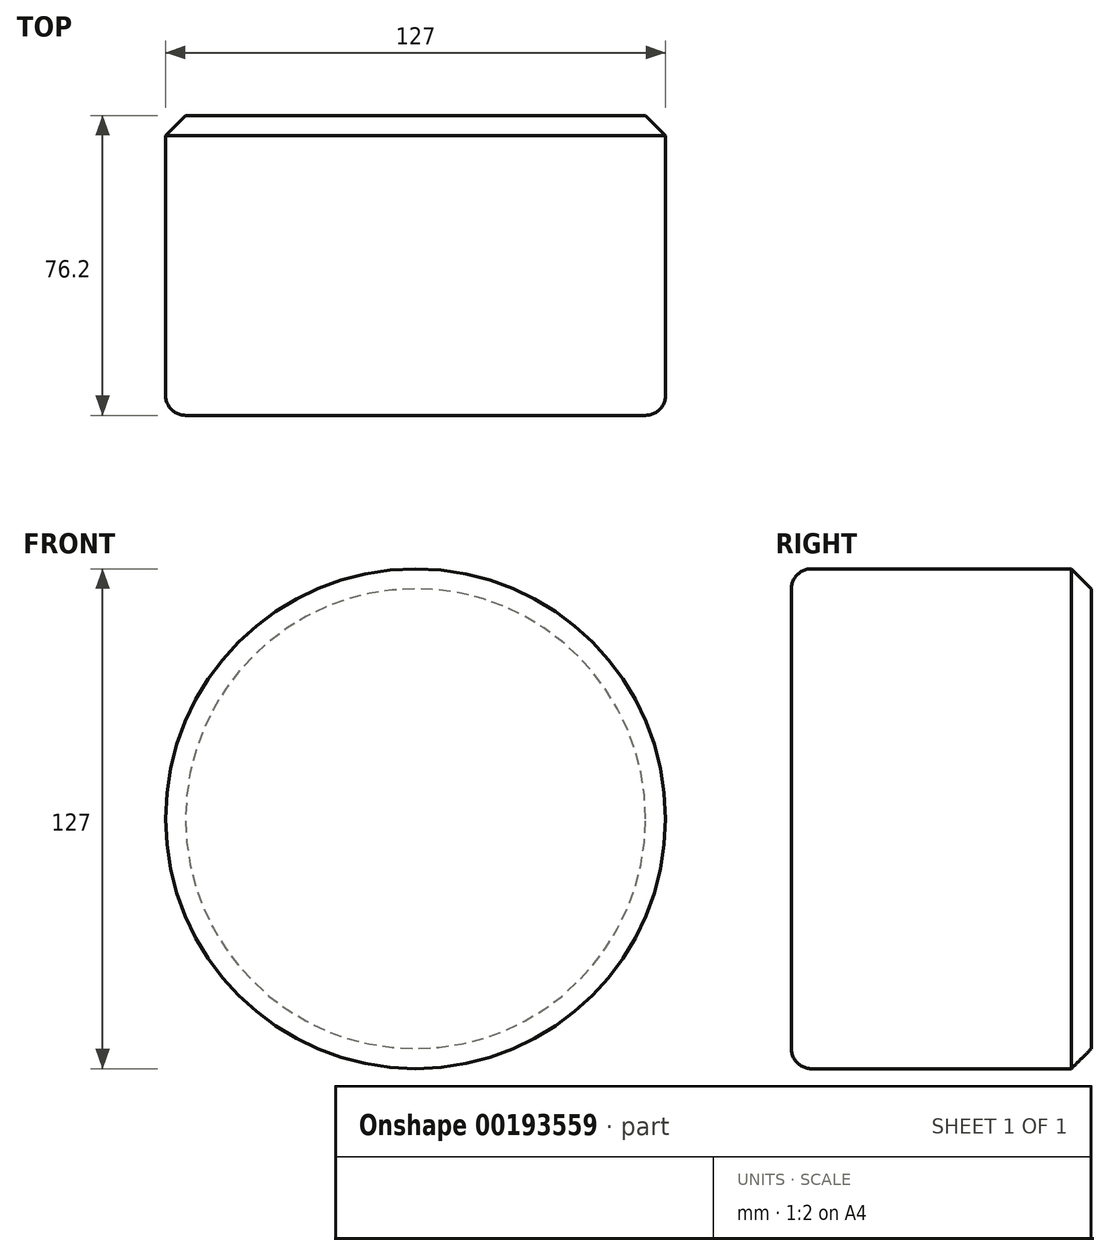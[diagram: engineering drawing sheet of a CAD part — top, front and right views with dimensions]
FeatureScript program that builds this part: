
annotation { "Feature Type Name" : "Feature", "Feature Type Description" : "" }
export const myFeature = defineFeature(function(context is Context, id is Id, definition is map)
    precondition{}
    {
        {
            var Q0;
            Q0=qCreatedBy(makeId("Front.planeOp"),FACE);
            var sketch = newSketch(context, id + "F0", { "sketchPlane" : qUnion([Q0])});
            skCircle(sketch, "E0", {"center": v(0, 0) * mm, "radius": 63.5 * mm});
            skSolve(sketch);
        }
        {
            var Q0;
            Q0=makeQuery(id+"F0.imprint","IMPRINT",FACE,{"disambiguationData":[TD([[makeQuery(id+"F0.imprint","IMPRINT",EDGE,{"derivedFrom":sQuery(id+"F0.wireOp",EDGE,"E0")}),1.0]])]});
            extrude(context, id + "F1", {"entities" : qUnion([Q0]), "depth" : 76.2 * mm});
        }
        {
            var Q0;
            Q0=qCreatedBy(makeId("Front.planeOp"),FACE);
            var sketch = newSketch(context, id + "F2", { "sketchPlane" : qUnion([Q0])});
            skCircle(sketch, "E1", {"center": v(0, 0) * mm, "radius": 30.95 * mm});
            skSolve(sketch);
        }
        {
            var Q0;
            Q0=sQuery(id+"F2.wireOp",EDGE,"E1");
            extrude(context, id + "F3", {"bodyType" : ToolBodyType.SURFACE, "surfaceEntities" : qUnion([Q0]), "depth" : 76.2 * mm});
        }
        {
            var Q0;
            Q0=qCreatedBy(makeId("Front.planeOp"),FACE);
            var sketch = newSketch(context, id + "F4", { "sketchPlane" : qUnion([Q0])});
            skCircle(sketch, "E2", {"center": v(0, 0) * mm, "radius": 9.2 * mm});
            skSolve(sketch);
        }
        {
            var Q0;
            Q0=sQuery(id+"F4.wireOp",EDGE,"E2");
            extrude(context, id + "F5", {"bodyType" : ToolBodyType.SURFACE, "surfaceEntities" : qUnion([Q0]), "depth" : 76.2 * mm});
        }
        {
            var Q0;
            Q0=makeQuery(id+"F1.opExtrude","CAP_EDGE",EDGE,{"disambiguationData":[OSD([sQuery(id+"F0.wireOp",EDGE,"E0")])],"isStart":false});
            fillet(context, id + "F6", {"entities" : qUnion([Q0]), "radius" : 5.08 * mm, "tangentPropagation" : true, "allowEdgeOverflow" : false});
        }
        {
            var Q0;
            Q0=makeQuery(id+"F1.opExtrude","CAP_EDGE",EDGE,{"disambiguationData":[OSD([sQuery(id+"F0.wireOp",EDGE,"E0")])],"isStart":true});
            chamfer(context, id + "F7", {"entities" : qUnion([Q0]), "width" : 5.08 * mm, "tangentPropagation" : true});
        }
    });
